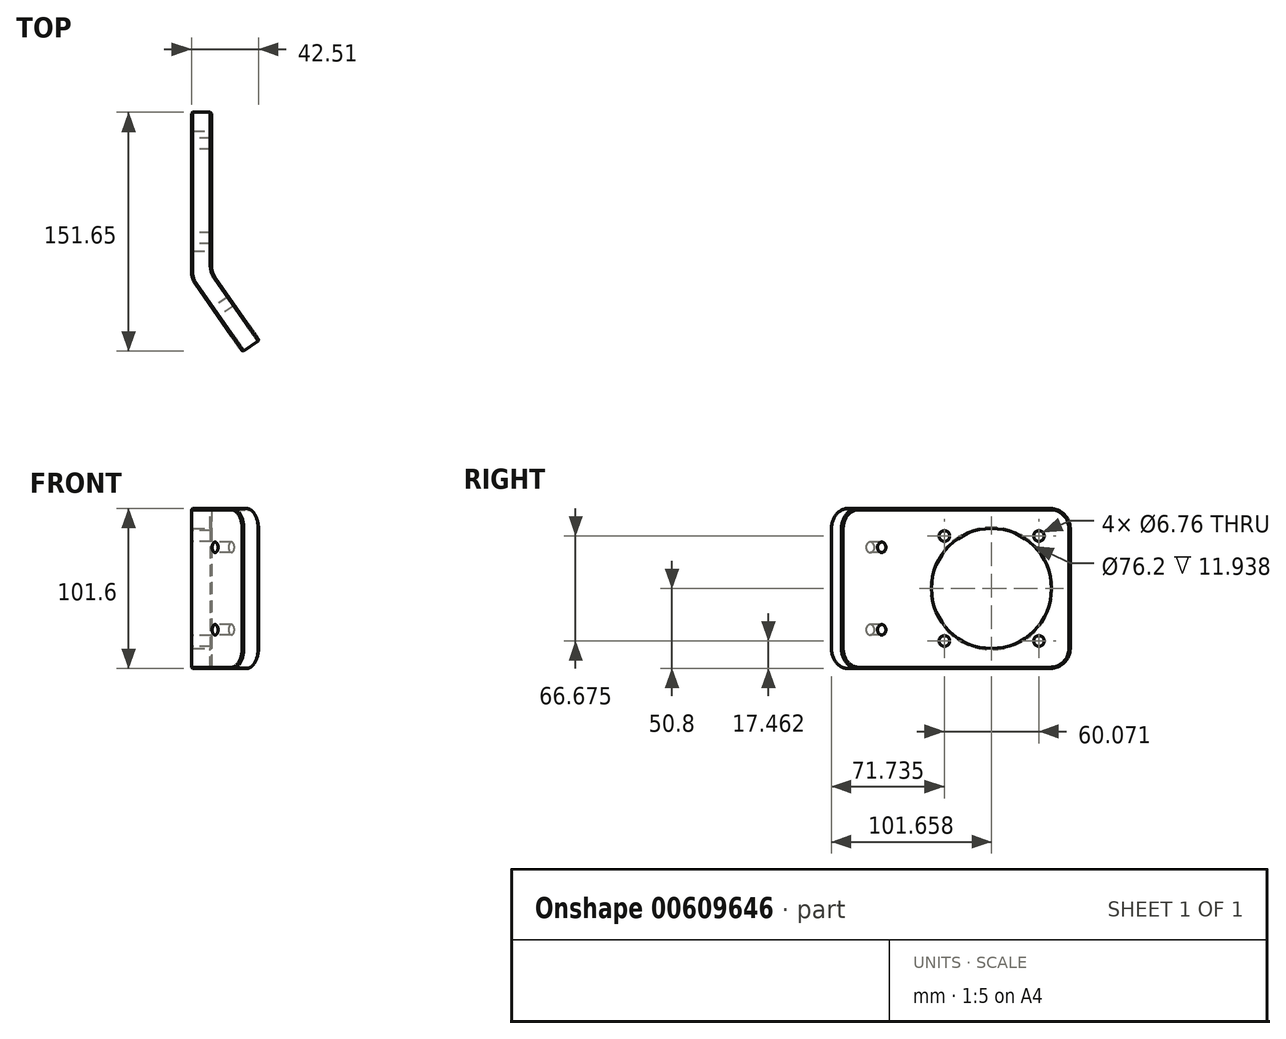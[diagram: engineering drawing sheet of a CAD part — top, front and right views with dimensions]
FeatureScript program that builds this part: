
annotation { "Feature Type Name" : "Feature", "Feature Type Description" : "" }
export const myFeature = defineFeature(function(context is Context, id is Id, definition is map)
    precondition{}
    {
        {
            var Q0;
            Q0=qCreatedBy(makeId("Top.planeOp"),FACE);
            var sketch = newSketch(context, id + "F0", { "sketchPlane" : qUnion([Q0])});
            skLineSegment(sketch, "E0", {"start": v(0, 58.79) * mm, "end": v(0, -42.81) * mm});
            skLineSegment(sketch, "E1", {"start": v(0, -42.81) * mm, "end": v(29.14, -84.43) * mm});
            skLineSegment(sketch, "E2.0", {"start": v(-12.7, -46.82) * mm, "end": v(19.84, -93.3) * mm});
            skLineSegment(sketch, "E2.1", {"start": v(-12.7, 58.79) * mm, "end": v(-12.7, -46.82) * mm});
            skLineSegment(sketch, "E3", {"start": v(-12.7, 58.79) * mm, "end": v(0, 58.79) * mm});
            skLineSegment(sketch, "E4", {"start": v(0, 58.79) * mm, "end": v(0, 58.79) * mm});
            skLineSegment(sketch, "E5", {"start": v(19.84, -93.3) * mm, "end": v(30.24, -86) * mm});
            skLineSegment(sketch, "E6", {"start": v(29.14, -84.43) * mm, "end": v(30.24, -86) * mm});
            skSolve(sketch);
        }
        {
            var Q0;
            Q0=makeQuery(id+"F0.imprint","IMPRINT",FACE,{"disambiguationData":[TD([[makeQuery(id+"F0.imprint","IMPRINT",EDGE,{"derivedFrom":sQuery(id+"F0.wireOp",EDGE,"E0")}),-1.0]])]});
            extrude(context, id + "F1", {"entities" : qUnion([Q0]), "depth" : 101.6 * mm, "offsetDistance" : 25.4 * mm, "symmetric" : true});
        }
        {
            var Q0;
            Q0=makeQuery(id+"F1.opExtrude","SWEPT_FACE",FACE,{"disambiguationData":[OSD([sQuery(id+"F0.wireOp",EDGE,"E0"),sQuery(id+"F0.wireOp",EDGE,"E4")])]});
            var sketch = newSketch(context, id + "F2", { "sketchPlane" : qUnion([Q0])});
            skPoint(sketch, "E7", {"position": v(38.95, 33.34) * mm});
            skPoint(sketch, "E8", {"position": v(38.95, -33.34) * mm});
            skPoint(sketch, "E9", {"position": v(-21.13, -33.34) * mm});
            skPoint(sketch, "E10", {"position": v(-21.13, 33.34) * mm});
            skSolve(sketch);
        }
        {
            var Q0;
            Q0=sQuery(id+"F2.wireOp",VERTEX,"E7");
            var Q1;
            Q1=sQuery(id+"F2.wireOp",VERTEX,"E8");
            var Q2;
            Q2=sQuery(id+"F2.wireOp",VERTEX,"E9");
            var Q3;
            Q3=sQuery(id+"F2.wireOp",VERTEX,"E10");
            var Q4;
            Q4=makeQuery(id+"F1.opExtrude","SWEPT_BODY",BODY,{"disambiguationData":[OSD([sQuery(id+"F0.wireOp",EDGE,"E0"),sQuery(id+"F0.wireOp",EDGE,"E1"),sQuery(id+"F0.wireOp",EDGE,"E2.0"),sQuery(id+"F0.wireOp",EDGE,"E2.1"),sQuery(id+"F0.wireOp",EDGE,"E3"),sQuery(id+"F0.wireOp",EDGE,"E4"),sQuery(id+"F0.wireOp",EDGE,"E5"),sQuery(id+"F0.wireOp",EDGE,"E6")])]});
            hole(context, id + "F3", {"style" : HoleStyle.SIMPLE, "endStyle" : HoleEndStyle.THROUGH, "standardTappedOrClearance" : lookupTablePath({ "standard" : "ANSI", "fit" : "Normal (ASME)", "size" : "1/4", "type" : "Clearance" }), "standardBlindInLast" : lookupTablePath({ "fit" : "Free", "standard" : "ANSI", "size" : "1/4", "type" : "Clearance" }), "holeDiameter" : 6.76 * mm, "majorDiameter" : 6.35 * mm, "isTappedThrough" : true, "tappedDepth" : 12.7 * mm, "tapClearance" : 3, "locations" : qUnion([Q0, Q1, Q2, Q3]), "scope" : qUnion([Q4])});
        }
        {
            var Q0;
            Q0=makeQuery(id+"F1.opExtrude","SWEPT_FACE",FACE,{"disambiguationData":[OSD([sQuery(id+"F0.wireOp",EDGE,"E0"),sQuery(id+"F0.wireOp",EDGE,"E4")])]});
            var sketch = newSketch(context, id + "F4", { "sketchPlane" : qUnion([Q0])});
            skCircle(sketch, "E11", {"center": v(8.8, 0) * mm, "radius": 38.1 * mm});
            skSolve(sketch);
        }
        {
            var Q0;
            Q0=makeQuery(id+"F4.imprint","IMPRINT",FACE,{"disambiguationData":[TD([[makeQuery(id+"F4.imprint","IMPRINT",EDGE,{"derivedFrom":sQuery(id+"F4.wireOp",EDGE,"E11")}),1.0]])]});
            extrude(context, id + "F5", {"entities" : qUnion([Q0]), "operationType" : NewBodyOperationType.REMOVE, "oppositeDirection" : true, "depth" : 13.46 * mm, "offsetDistance" : 25.4 * mm});
        }
        {
            var Q0;
            Q0=makeQuery(id+"F1.opExtrude","CAP_EDGE",EDGE,{"disambiguationData":[OSD([sQuery(id+"F0.wireOp",EDGE,"E3")])],"isStart":true});
            var Q1;
            Q1=makeQuery(id+"F1.opExtrude","CAP_EDGE",EDGE,{"disambiguationData":[OSD([sQuery(id+"F0.wireOp",EDGE,"E3")])],"isStart":false});
            var Q2;
            Q2=makeQuery(id+"F1.opExtrude","CAP_EDGE",EDGE,{"disambiguationData":[OSD([sQuery(id+"F0.wireOp",EDGE,"E5")])],"isStart":false});
            var Q3;
            Q3=makeQuery(id+"F1.opExtrude","CAP_EDGE",EDGE,{"disambiguationData":[OSD([sQuery(id+"F0.wireOp",EDGE,"E5")])],"isStart":true});
            fillet(context, id + "F6", {"entities" : qUnion([Q0, Q1, Q2, Q3]), "radius" : 12.7 * mm, "tangentPropagation" : true, "allowEdgeOverflow" : false});
        }
        {
            var Q0;
            Q0=makeQuery(id+"F1.opExtrude","SWEPT_EDGE",EDGE,{"disambiguationData":[OSD([sQuery(id+"F0.wireOp",EDGE,"E0"),sQuery(id+"F0.wireOp",EDGE,"E1")])]});
            var Q1;
            Q1=makeQuery(id+"F1.opExtrude","SWEPT_EDGE",EDGE,{"disambiguationData":[OSD([sQuery(id+"F0.wireOp",EDGE,"E2.0"),sQuery(id+"F0.wireOp",EDGE,"E2.1")])]});
            fillet(context, id + "F7", {"entities" : qUnion([Q0, Q1]), "radius" : 12.7 * mm, "tangentPropagation" : true, "allowEdgeOverflow" : false});
        }
        {
            var Q0;
            Q0=makeQuery(id+"F5.boolean.opBoolean","COPY",EDGE,{"derivedFrom":makeQuery(id+"F5.opExtrude","CAP_EDGE",EDGE,{"disambiguationData":[OSD([sQuery(id+"F4.wireOp",EDGE,"E11")])],"isStart":true})});
            var Q1;
            Q1=makeQuery(id+"F5.boolean.opBoolean","INTERSECT",EDGE,{"derivedFrom":[makeQuery(id+"F1.opExtrude","SWEPT_FACE",FACE,{"disambiguationData":[OSD([sQuery(id+"F0.wireOp",EDGE,"E2.1")])]}),makeQuery(id+"F5.opExtrude","SWEPT_FACE",FACE,{"disambiguationData":[OSD([sQuery(id+"F4.wireOp",EDGE,"E11")])]})]});
            var Q2;
            Q2=makeQuery(id+"F1.opExtrude","SWEPT_EDGE",EDGE,{"disambiguationData":[OSD([sQuery(id+"F0.wireOp",EDGE,"E0"),sQuery(id+"F0.wireOp",EDGE,"E3")])]});
            var Q3;
            Q3=makeQuery(id+"F6.opFillet","BLEND_EDGE",EDGE,{"blendedFrom":[makeQuery(id+"F1.opExtrude","CAP_EDGE",EDGE,{"disambiguationData":[OSD([sQuery(id+"F0.wireOp",EDGE,"E3")])],"isStart":true}),makeQuery(id+"F1.opExtrude","SWEPT_FACE",FACE,{"disambiguationData":[OSD([sQuery(id+"F0.wireOp",EDGE,"E0")])]})],"blendedInto":[makeQuery(id+"F1.opExtrude","SWEPT_FACE",FACE,{"disambiguationData":[OSD([sQuery(id+"F0.wireOp",EDGE,"E0")])]})]});
            var Q4;
            Q4=makeQuery(id+"F1.opExtrude","CAP_EDGE",EDGE,{"disambiguationData":[OSD([sQuery(id+"F0.wireOp",EDGE,"E0")])],"isStart":true});
            var Q5;
            {var subQ0=sQuery(id+"F0.wireOp",EDGE,"E1");var subQ1=sQuery(id+"F0.wireOp",EDGE,"E0");Q5=makeQuery(id+"F7.opFillet","BLEND_EDGE",EDGE,{"blendedFrom":[makeQuery(id+"F1.opExtrude","SWEPT_EDGE",EDGE,{"disambiguationData":[OSD([subQ1,subQ0])]}),makeQuery(id+"F1.opExtrude","CAP_FACE",FACE,{"disambiguationData":[OSD([subQ1,subQ0,sQuery(id+"F0.wireOp",EDGE,"E2.0"),sQuery(id+"F0.wireOp",EDGE,"E2.1"),sQuery(id+"F0.wireOp",EDGE,"E3"),sQuery(id+"F0.wireOp",EDGE,"E5"),sQuery(id+"F0.wireOp",EDGE,"E6")])],"isStart":true})],"blendedInto":[makeQuery(id+"F1.opExtrude","CAP_FACE",FACE,{"disambiguationData":[OSD([subQ1,subQ0,sQuery(id+"F0.wireOp",EDGE,"E2.0"),sQuery(id+"F0.wireOp",EDGE,"E2.1"),sQuery(id+"F0.wireOp",EDGE,"E3"),sQuery(id+"F0.wireOp",EDGE,"E5"),sQuery(id+"F0.wireOp",EDGE,"E6")])],"isStart":true})]});}
            var Q6;
            Q6=makeQuery(id+"F6.opFillet","BLEND_EDGE",EDGE,{"blendedFrom":[makeQuery(id+"F1.opExtrude","CAP_EDGE",EDGE,{"disambiguationData":[OSD([sQuery(id+"F0.wireOp",EDGE,"E5")])],"isStart":true}),makeQuery(id+"F1.opExtrude","SWEPT_FACE",FACE,{"disambiguationData":[OSD([sQuery(id+"F0.wireOp",EDGE,"E1"),sQuery(id+"F0.wireOp",EDGE,"E6")])]})],"blendedInto":[makeQuery(id+"F1.opExtrude","SWEPT_FACE",FACE,{"disambiguationData":[OSD([sQuery(id+"F0.wireOp",EDGE,"E1"),sQuery(id+"F0.wireOp",EDGE,"E6")])]})]});
            var Q7;
            Q7=makeQuery(id+"F1.opExtrude","CAP_EDGE",EDGE,{"disambiguationData":[OSD([sQuery(id+"F0.wireOp",EDGE,"E1"),sQuery(id+"F0.wireOp",EDGE,"E6")])],"isStart":true});
            var Q8;
            Q8=makeQuery(id+"F1.opExtrude","SWEPT_EDGE",EDGE,{"disambiguationData":[OSD([sQuery(id+"F0.wireOp",EDGE,"E5"),sQuery(id+"F0.wireOp",EDGE,"E6")])]});
            var Q9;
            Q9=makeQuery(id+"F6.opFillet","BLEND_EDGE",EDGE,{"blendedFrom":[makeQuery(id+"F1.opExtrude","CAP_EDGE",EDGE,{"disambiguationData":[OSD([sQuery(id+"F0.wireOp",EDGE,"E5")])],"isStart":false}),makeQuery(id+"F1.opExtrude","SWEPT_FACE",FACE,{"disambiguationData":[OSD([sQuery(id+"F0.wireOp",EDGE,"E1"),sQuery(id+"F0.wireOp",EDGE,"E6")])]})],"blendedInto":[makeQuery(id+"F1.opExtrude","SWEPT_FACE",FACE,{"disambiguationData":[OSD([sQuery(id+"F0.wireOp",EDGE,"E1"),sQuery(id+"F0.wireOp",EDGE,"E6")])]})]});
            var Q10;
            Q10=makeQuery(id+"F1.opExtrude","CAP_EDGE",EDGE,{"disambiguationData":[OSD([sQuery(id+"F0.wireOp",EDGE,"E1"),sQuery(id+"F0.wireOp",EDGE,"E6")])],"isStart":false});
            var Q11;
            Q11=makeQuery(id+"F6.opFillet","BLEND_EDGE",EDGE,{"blendedFrom":[makeQuery(id+"F1.opExtrude","CAP_EDGE",EDGE,{"disambiguationData":[OSD([sQuery(id+"F0.wireOp",EDGE,"E3")])],"isStart":false}),makeQuery(id+"F1.opExtrude","SWEPT_FACE",FACE,{"disambiguationData":[OSD([sQuery(id+"F0.wireOp",EDGE,"E2.1")])]})],"blendedInto":[makeQuery(id+"F1.opExtrude","SWEPT_FACE",FACE,{"disambiguationData":[OSD([sQuery(id+"F0.wireOp",EDGE,"E2.1")])]})]});
            var Q12;
            Q12=makeQuery(id+"F1.opExtrude","CAP_EDGE",EDGE,{"disambiguationData":[OSD([sQuery(id+"F0.wireOp",EDGE,"E2.1")])],"isStart":false});
            var Q13;
            Q13=makeQuery(id+"F1.opExtrude","SWEPT_EDGE",EDGE,{"disambiguationData":[OSD([sQuery(id+"F0.wireOp",EDGE,"E2.1"),sQuery(id+"F0.wireOp",EDGE,"E3")])]});
            chamfer(context, id + "F8", {"entities" : qUnion([Q0, Q1, Q2, Q3, Q4, Q5, Q6, Q7, Q8, Q9, Q10, Q11, Q12, Q13]), "width" : 0.76 * mm, "tangentPropagation" : true});
        }
        {
            var Q0;
            Q0=makeQuery(id+"F1.opExtrude","SWEPT_FACE",FACE,{"disambiguationData":[OSD([sQuery(id+"F0.wireOp",EDGE,"E1"),sQuery(id+"F0.wireOp",EDGE,"E6")])]});
            var sketch = newSketch(context, id + "F9", { "sketchPlane" : qUnion([Q0])});
            skLineSegment(sketch, "E12", {"start": v(0, 26.2) * mm, "end": v(0, -26.2) * mm, "construction": true});
            skLineSegment(sketch, "E13.bottom", {"start": v(0, 26.2) * mm, "end": v(-57.15, 26.2) * mm, "construction": true});
            skLineSegment(sketch, "E13.top", {"start": v(0, -26.2) * mm, "end": v(-57.15, -26.2) * mm, "construction": true});
            skLineSegment(sketch, "E13.right", {"start": v(-57.15, 26.2) * mm, "end": v(-57.15, -26.2) * mm, "construction": true});
            skSolve(sketch);
        }
        {
            var Q0;
            Q0=sQuery(id+"F9.wireOp",VERTEX,"E13.top.end");
            var Q1;
            Q1=sQuery(id+"F9.wireOp",VERTEX,"E13.bottom.end");
            var Q2;
            Q2=makeQuery(id+"F1.opExtrude","SWEPT_BODY",BODY,{"disambiguationData":[OSD([sQuery(id+"F0.wireOp",EDGE,"E0"),sQuery(id+"F0.wireOp",EDGE,"E1"),sQuery(id+"F0.wireOp",EDGE,"E2.0"),sQuery(id+"F0.wireOp",EDGE,"E2.1"),sQuery(id+"F0.wireOp",EDGE,"E3"),sQuery(id+"F0.wireOp",EDGE,"E5"),sQuery(id+"F0.wireOp",EDGE,"E6")])]});
            hole(context, id + "F10", {"style" : HoleStyle.SIMPLE, "endStyle" : HoleEndStyle.THROUGH, "standardTappedOrClearance" : lookupTablePath({ "standard" : "ANSI", "engagement" : "75%", "pitch" : "18 tpi", "size" : "5/16", "type" : "Tapped" }), "standardBlindInLast" : lookupTablePath({ "standard" : "ANSI", "engagement" : "75%", "pitch" : "18 tpi", "size" : "5/16", "type" : "Tapped" }), "holeDiameter" : 6.53 * mm, "majorDiameter" : 7.94 * mm, "showTappedDepth" : true, "isTappedThrough" : true, "tappedDepth" : 12.7 * mm, "tapClearance" : 3, "locations" : qUnion([Q0, Q1]), "scope" : qUnion([Q2])});
        }
    });
